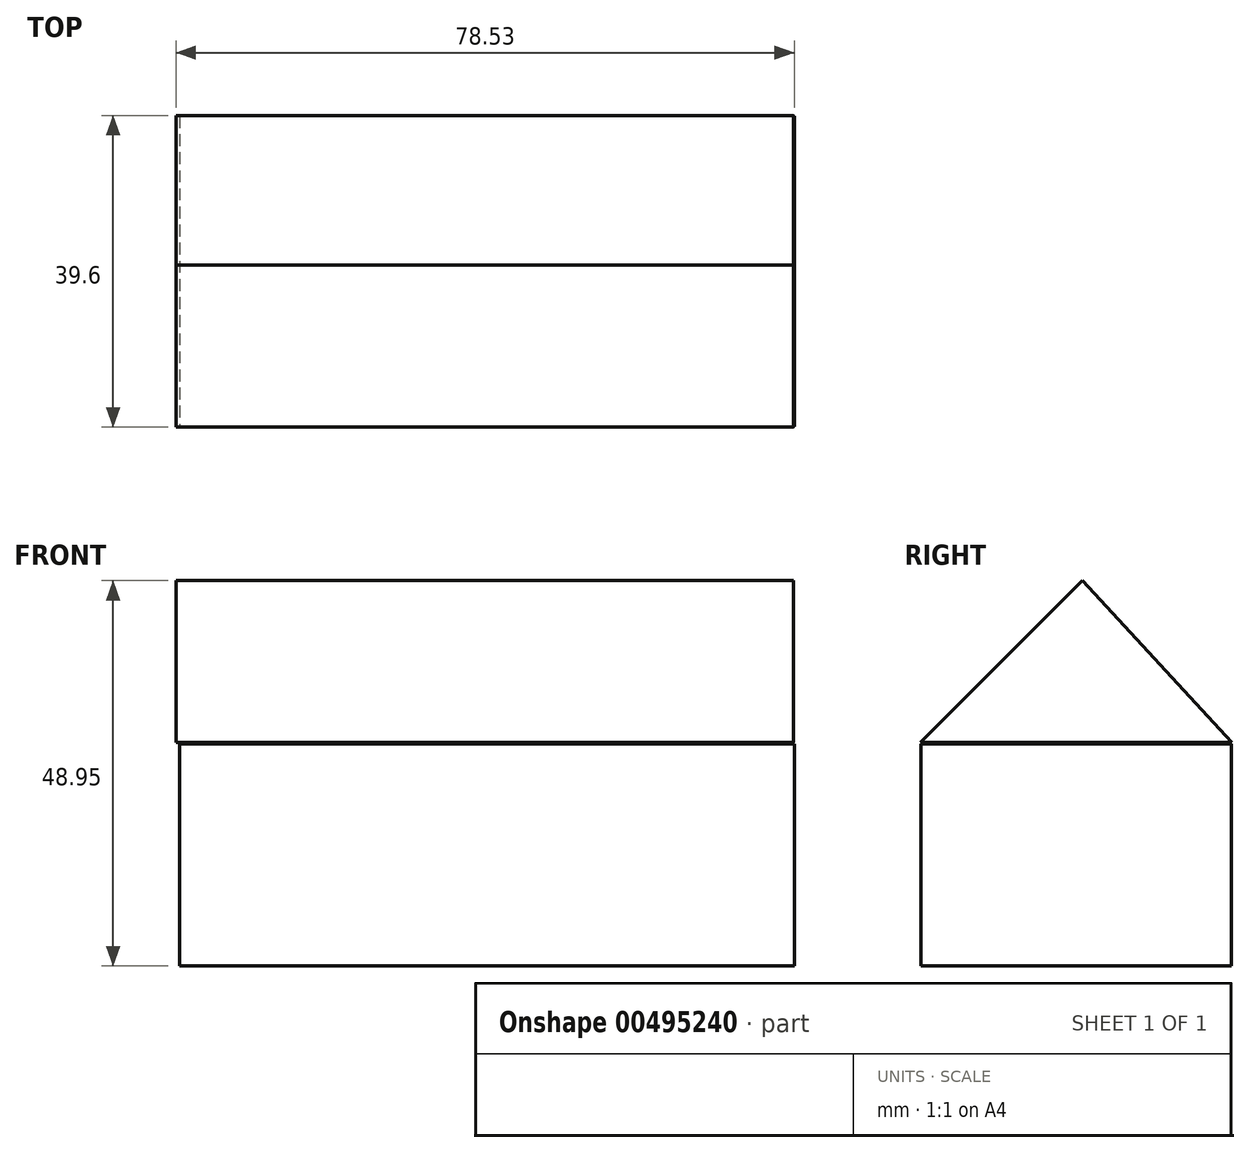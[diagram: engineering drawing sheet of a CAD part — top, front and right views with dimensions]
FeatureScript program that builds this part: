
annotation { "Feature Type Name" : "Feature", "Feature Type Description" : "" }
export const myFeature = defineFeature(function(context is Context, id is Id, definition is map)
    precondition{}
    {
        {
            var Q0;
            Q0=qCreatedBy(makeId("Top.planeOp"),FACE);
            var sketch = newSketch(context, id + "F0", { "sketchPlane" : qUnion([Q0])});
            skLineSegment(sketch, "E0.bottom", {"start": v(-38.78, 18.9) * mm, "end": v(39.33, 18.9) * mm});
            skLineSegment(sketch, "E0.top", {"start": v(-38.78, -20.56) * mm, "end": v(39.33, -20.56) * mm});
            skLineSegment(sketch, "E0.left", {"start": v(-38.78, 18.9) * mm, "end": v(-38.78, -20.56) * mm});
            skLineSegment(sketch, "E0.right", {"start": v(39.33, 18.9) * mm, "end": v(39.33, -20.56) * mm});
            skSolve(sketch);
        }
        {
            var Q0;
            Q0 = qSketchRegion(id + "F0", true);
            extrude(context, id + "F1", {"entities" : qUnion([Q0]), "depth" : 28.2 * mm, "offsetDistance" : 25 * mm});
        }
        {
            var Q0;
            Q0=qCreatedBy(makeId("Right.planeOp"),FACE);
            var sketch = newSketch(context, id + "F2", { "sketchPlane" : qUnion([Q0])});
            skLineSegment(sketch, "E1", {"start": v(0, 48.95) * mm, "end": v(-20.62, 28.4) * mm});
            skLineSegment(sketch, "E2", {"start": v(-20.62, 28.4) * mm, "end": v(18.98, 28.4) * mm});
            skLineSegment(sketch, "E3", {"start": v(18.98, 28.4) * mm, "end": v(0, 48.95) * mm});
            skSolve(sketch);
        }
        {
            var Q0;
            Q0=makeQuery(id+"F2.imprint","IMPRINT",FACE,{"disambiguationData":[TD([[makeQuery(id+"F2.imprint","IMPRINT",EDGE,{"derivedFrom":sQuery(id+"F2.wireOp",EDGE,"E1")}),1.0]])]});
            extrude(context, id + "F3", {"entities" : qUnion([Q0]), "endBound" : BoundingType.SYMMETRIC, "depth" : 78.4 * mm, "offsetDistance" : 25 * mm});
        }
    });
